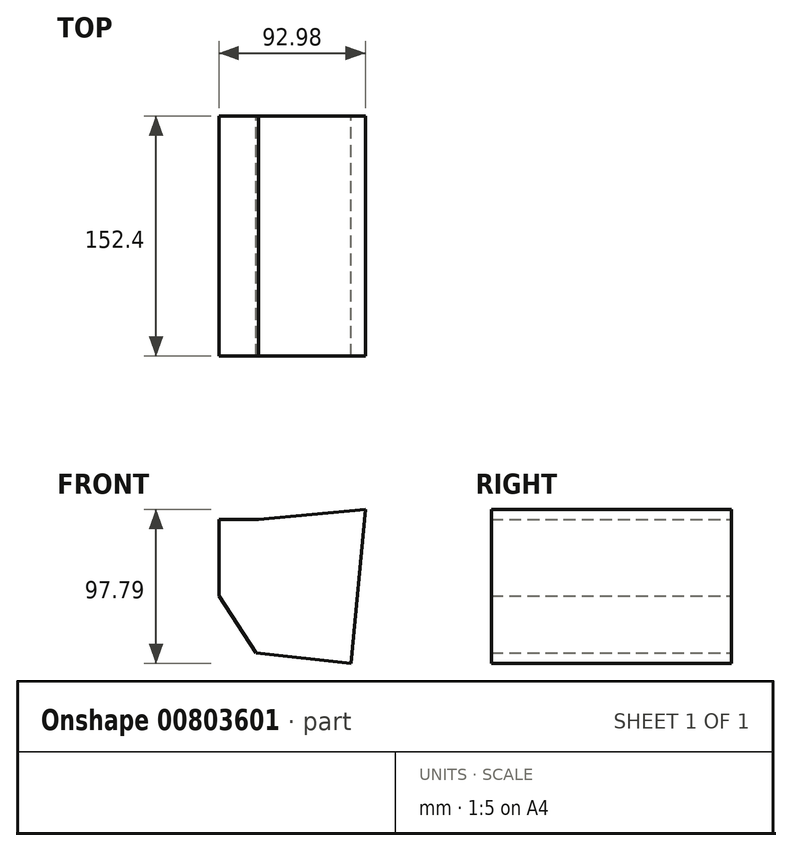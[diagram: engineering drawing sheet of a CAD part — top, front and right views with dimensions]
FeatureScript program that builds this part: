
annotation { "Feature Type Name" : "Feature", "Feature Type Description" : "" }
export const myFeature = defineFeature(function(context is Context, id is Id, definition is map)
    precondition{}
    {
        {
            var Q0;
            Q0=qCreatedBy(makeId("Front.planeOp"),FACE);
            var sketch = newSketch(context, id + "F0", { "sketchPlane" : qUnion([Q0])});
            skLineSegment(sketch, "E0", {"start": v(-24.59, 48.56) * mm, "end": v(-49.66, 48.56) * mm});
            skLineSegment(sketch, "E1", {"start": v(-49.66, 48.56) * mm, "end": v(-49.66, 0) * mm});
            skLineSegment(sketch, "E2", {"start": v(-49.66, 0) * mm, "end": v(0, 0) * mm});
            skLineSegment(sketch, "E3", {"start": v(0, 0) * mm, "end": v(-24.59, 48.56) * mm});
            skLineSegment(sketch, "E4", {"start": v(43.32, 54.75) * mm, "end": v(-24.59, 48.56) * mm});
            skLineSegment(sketch, "E5", {"start": v(34.09, -43.04) * mm, "end": v(43.32, 54.75) * mm});
            skLineSegment(sketch, "E6", {"start": v(0, 0) * mm, "end": v(34.09, -43.04) * mm});
            skLineSegment(sketch, "E7", {"start": v(-25.97, -36.3) * mm, "end": v(-49.66, 0) * mm});
            skLineSegment(sketch, "E8", {"start": v(34.09, -43.04) * mm, "end": v(-25.97, -36.3) * mm});
            skLineSegment(sketch, "E9", {"start": v(-25.97, -36.3) * mm, "end": v(0, 0) * mm});
            skLineSegment(sketch, "E10", {"start": v(39.27, 11.88) * mm, "end": v(9.36, 51.65) * mm});
            skLineSegment(sketch, "E11", {"start": v(9.36, 51.65) * mm, "end": v(0, 0) * mm});
            skLineSegment(sketch, "E12", {"start": v(39.27, 11.88) * mm, "end": v(0, 0) * mm});
            skSolve(sketch);
        }
        {
            var Q0;
            {var subQ0=sQuery(id+"F0.wireOp",EDGE,"E3");Q0=makeQuery(id+"F0.imprint","IMPRINT",FACE,{"disambiguationData":[TD([[makeQuery(id+"F0.imprint","IMPRINT",EDGE,{"derivedFrom":subQ0}),-1.0]])]});}
            var Q1;
            Q1=makeQuery(id+"F0.imprint","IMPRINT",FACE,{"disambiguationData":[TD([[makeQuery(id+"F0.imprint","IMPRINT",EDGE,{"derivedFrom":sQuery(id+"F0.wireOp",EDGE,"E0")}),1.0]])]});
            var Q2;
            Q2=makeQuery(id+"F0.imprint","IMPRINT",FACE,{"disambiguationData":[TD([[makeQuery(id+"F0.imprint","IMPRINT",EDGE,{"derivedFrom":sQuery(id+"F0.wireOp",EDGE,"E2")}),-1.0]])]});
            var Q3;
            Q3=makeQuery(id+"F0.imprint","IMPRINT",FACE,{"disambiguationData":[TD([[makeQuery(id+"F0.imprint","IMPRINT",EDGE,{"derivedFrom":sQuery(id+"F0.wireOp",EDGE,"E10")}),1.0]])]});
            var Q4;
            {var subQ3=sQuery(id+"F0.wireOp",EDGE,"E10");Q4=makeQuery(id+"F0.imprint","IMPRINT",FACE,{"disambiguationData":[TD([[makeQuery(id+"F0.imprint","IMPRINT",EDGE,{"derivedFrom":subQ3}),-1.0]])]});}
            var Q5;
            {var subQ0=sQuery(id+"F0.wireOp",EDGE,"E6");Q5=makeQuery(id+"F0.imprint","IMPRINT",FACE,{"disambiguationData":[TD([[makeQuery(id+"F0.imprint","IMPRINT",EDGE,{"derivedFrom":subQ0}),1.0]])]});}
            var Q6;
            Q6=makeQuery(id+"F0.imprint","IMPRINT",FACE,{"disambiguationData":[TD([[makeQuery(id+"F0.imprint","IMPRINT",EDGE,{"derivedFrom":sQuery(id+"F0.wireOp",EDGE,"E6")}),-1.0]])]});
            extrude(context, id + "F1", {"entities" : qUnion([Q0, Q1, Q2, Q3, Q4, Q5, Q6]), "depth" : 152.4 * mm, "offsetDistance" : 25.4 * mm});
        }
    });
